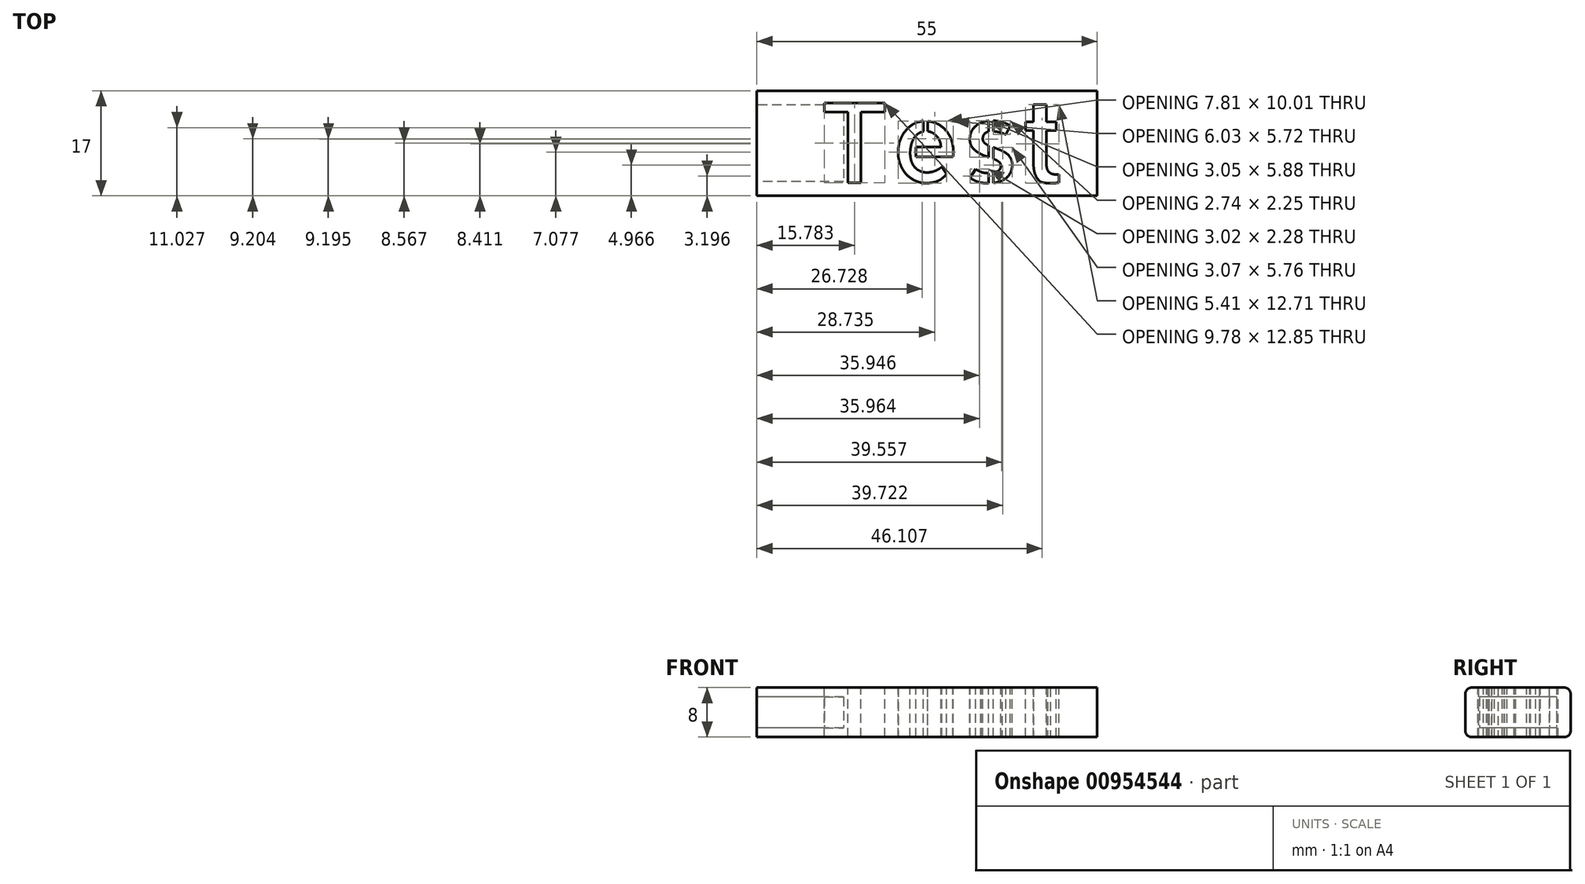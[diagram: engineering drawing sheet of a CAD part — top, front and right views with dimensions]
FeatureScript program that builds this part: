
annotation { "Feature Type Name" : "Feature", "Feature Type Description" : "" }
export const myFeature = defineFeature(function(context is Context, id is Id, definition is map)
    precondition{}
    {
        {
            var Q0;
            Q0=qCreatedBy(makeId("Front.planeOp"),FACE);
            var sketch = newSketch(context, id + "F0", { "sketchPlane" : qUnion([Q0])});
            skLineSegment(sketch, "E0.bottom", {"start": v(-7.5, 4) * mm, "end": v(7.5, 4) * mm});
            skLineSegment(sketch, "E0.top", {"start": v(-7.5, -4) * mm, "end": v(7.5, -4) * mm});
            skLineSegment(sketch, "E0.left", {"start": v(-8.5, 3) * mm, "end": v(-8.5, -3) * mm});
            skLineSegment(sketch, "E0.right", {"start": v(8.5, 3) * mm, "end": v(8.5, -3) * mm});
            skPoint(sketch, "E1.visualSharp", {"position": v(-8.5, 4) * mm});
            skArc(sketch, "E1.filletArc", {"start": v(-7.5, 4) * mm, "mid": v(-8.2, 3.7) * mm, "end": v(-8.5, 3) * mm});
            skPoint(sketch, "E2.visualSharp", {"position": v(-8.5, -4) * mm});
            skArc(sketch, "E2.filletArc", {"start": v(-8.5, -3) * mm, "mid": v(-8.2, -3.7) * mm, "end": v(-7.5, -4) * mm});
            skPoint(sketch, "E3.visualSharp", {"position": v(8.5, 4) * mm});
            skArc(sketch, "E3.filletArc", {"start": v(8.5, 3) * mm, "mid": v(8.2, 3.7) * mm, "end": v(7.5, 4) * mm});
            skPoint(sketch, "E4.visualSharp", {"position": v(8.5, -4) * mm});
            skArc(sketch, "E4.filletArc", {"start": v(7.5, -4) * mm, "mid": v(8.2, -3.7) * mm, "end": v(8.5, -3) * mm});
            skSolve(sketch);
        }
        {
            var Q0;
            Q0 = qSketchRegion(id + "F0", true);
            extrude(context, id + "F1", {"entities" : qUnion([Q0]), "depth" : 55 * mm, "offsetDistance" : 25 * mm});
        }
        {
            var Q0;
            Q0=makeQuery(id+"F1.opExtrude","CAP_FACE",FACE,{"disambiguationData":[OSD([sQuery(id+"F0.wireOp",EDGE,"E0.bottom"),sQuery(id+"F0.wireOp",EDGE,"E0.top"),sQuery(id+"F0.wireOp",EDGE,"E0.left"),sQuery(id+"F0.wireOp",EDGE,"E0.right"),sQuery(id+"F0.wireOp",EDGE,"E1.filletArc"),sQuery(id+"F0.wireOp",EDGE,"E2.filletArc"),sQuery(id+"F0.wireOp",EDGE,"E3.filletArc"),sQuery(id+"F0.wireOp",EDGE,"E4.filletArc")])],"isStart":false});
            var sketch = newSketch(context, id + "F2", { "sketchPlane" : qUnion([Q0])});
            skLineSegment(sketch, "E5.bottom", {"start": v(-6.2, 2.5) * mm, "end": v(6.2, 2.5) * mm});
            skLineSegment(sketch, "E5.top", {"start": v(-6.2, -2.5) * mm, "end": v(6.2, -2.5) * mm});
            skLineSegment(sketch, "E5.left", {"start": v(-6.2, 2.5) * mm, "end": v(-6.2, -2.5) * mm});
            skLineSegment(sketch, "E5.right", {"start": v(6.2, 2.5) * mm, "end": v(6.2, -2.5) * mm});
            skSolve(sketch);
        }
        {
            var Q0;
            Q0 = qSketchRegion(id + "F2", true);
            extrude(context, id + "F3", {"entities" : qUnion([Q0]), "operationType" : NewBodyOperationType.REMOVE, "oppositeDirection" : true, "depth" : 14 * mm, "offsetDistance" : 25 * mm});
        }
        {
            var Q0;
            Q0=makeQuery(id+"F1.opExtrude","SWEPT_BODY",BODY,{"disambiguationData":[OSD([sQuery(id+"F0.wireOp",EDGE,"E0.bottom"),sQuery(id+"F0.wireOp",EDGE,"E0.top"),sQuery(id+"F0.wireOp",EDGE,"E0.left"),sQuery(id+"F0.wireOp",EDGE,"E0.right"),sQuery(id+"F0.wireOp",EDGE,"E1.filletArc"),sQuery(id+"F0.wireOp",EDGE,"E2.filletArc"),sQuery(id+"F0.wireOp",EDGE,"E3.filletArc"),sQuery(id+"F0.wireOp",EDGE,"E4.filletArc")])]});
            var Q1;
            Q1=makeQuery(id+"F1.opExtrude","CAP_EDGE",EDGE,{"disambiguationData":[OSD([sQuery(id+"F0.wireOp",EDGE,"E0.left")])],"isStart":true});
            transform(context, id + "F4", {"entities" : qUnion([Q0]), "transformType" : TransformType.ROTATION, "transformAxis" : qUnion([Q1]), "angle" : 90 * degree, "makeCopy" : false});
        }
        {
            var Q0;
            Q0=makeQuery(id+"F1.opExtrude","SWEPT_FACE",FACE,{"disambiguationData":[OSD([sQuery(id+"F0.wireOp",EDGE,"E0.bottom")])]});
            var sketch = newSketch(context, id + "F5", { "sketchPlane" : qUnion([Q0])});
            skText(sketch, "E6", { "text": "Test\n", "fontName": "AllertaStencil-Regular.ttf"});
            const initialGuessF5  = {"E6": [-0.0535, -0.01486, 1, 0, 0.01286]};
            skSetInitialGuess(sketch, initialGuessF5);
            skSolve(sketch);
        }
        {
            var Q0;
            Q0 = qSketchRegion(id + "F5", true);
            extrude(context, id + "F6", {"entities" : qUnion([Q0]), "operationType" : NewBodyOperationType.REMOVE, "oppositeDirection" : true, "depth" : 25 * mm, "offsetDistance" : 25 * mm});
        }
    });
